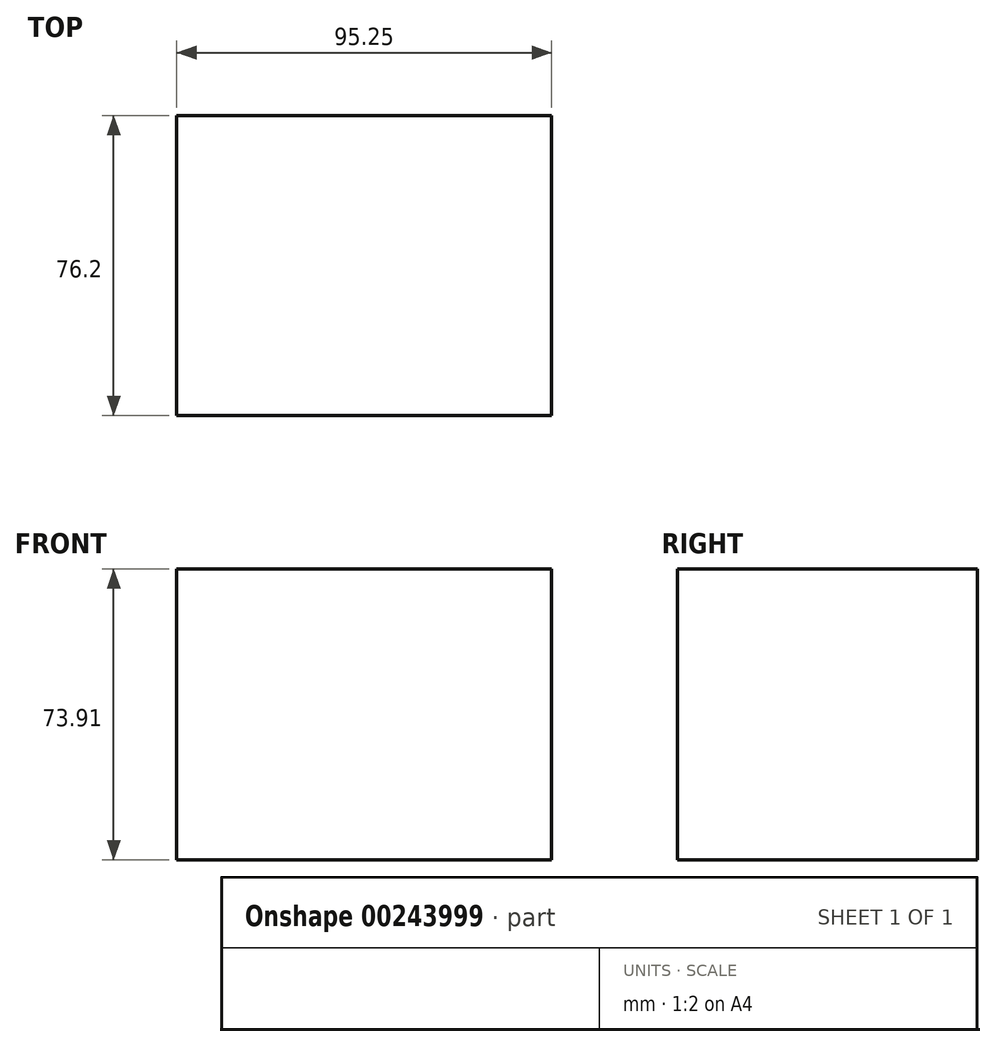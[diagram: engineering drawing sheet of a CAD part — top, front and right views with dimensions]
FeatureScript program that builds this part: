
annotation { "Feature Type Name" : "Feature", "Feature Type Description" : "" }
export const myFeature = defineFeature(function(context is Context, id is Id, definition is map)
    precondition{}
    {
        {
            var Q0;
            Q0=qCreatedBy(makeId("Top.planeOp"),FACE);
            var sketch = newSketch(context, id + "F0", { "sketchPlane" : qUnion([Q0])});
            skLineSegment(sketch, "E0.bottom", {"start": v(-46.28, 39.59) * mm, "end": v(48.97, 39.59) * mm});
            skLineSegment(sketch, "E0.top", {"start": v(-46.28, -36.61) * mm, "end": v(48.97, -36.61) * mm});
            skLineSegment(sketch, "E0.left", {"start": v(-46.28, 39.59) * mm, "end": v(-46.28, -36.61) * mm});
            skLineSegment(sketch, "E0.right", {"start": v(48.97, 39.59) * mm, "end": v(48.97, -36.61) * mm});
            skSolve(sketch);
        }
        {
            var Q0;
            Q0 = qSketchRegion(id + "F0", true);
            extrude(context, id + "F1", {"entities" : qUnion([Q0]), "depth" : 73.9 * mm});
        }
    });
